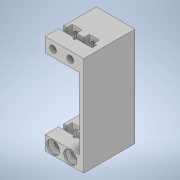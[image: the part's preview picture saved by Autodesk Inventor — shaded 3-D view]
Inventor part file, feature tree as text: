
AUTODESK INVENTOR PART (.ipt)
format: ipt  version: 2020 (Build 240168000, 168)  size: 202,240 bytes
history: native  units: mm
features: other x3, projected_geometry x2, extrude x1, sketch x1
ambient origin geometry x8: Origin, YZ Plane, XZ Plane, XY Plane, X Axis, Y Axis, Z Axis, Center Point
bodies: Solide2 (feature_tree)
feature tree (7):
  other  "servo_holder.ipt"
  extrude  "Extrusion6"  Depth=10.0mm
  other  "Solide1::servo_holder.ipt"
  other  "FonctionRepérage2"
  sketch  "Esquisse7"
  projected_geometry  "Boucle projetée2"
  projected_geometry  "Boucle projetée3"
